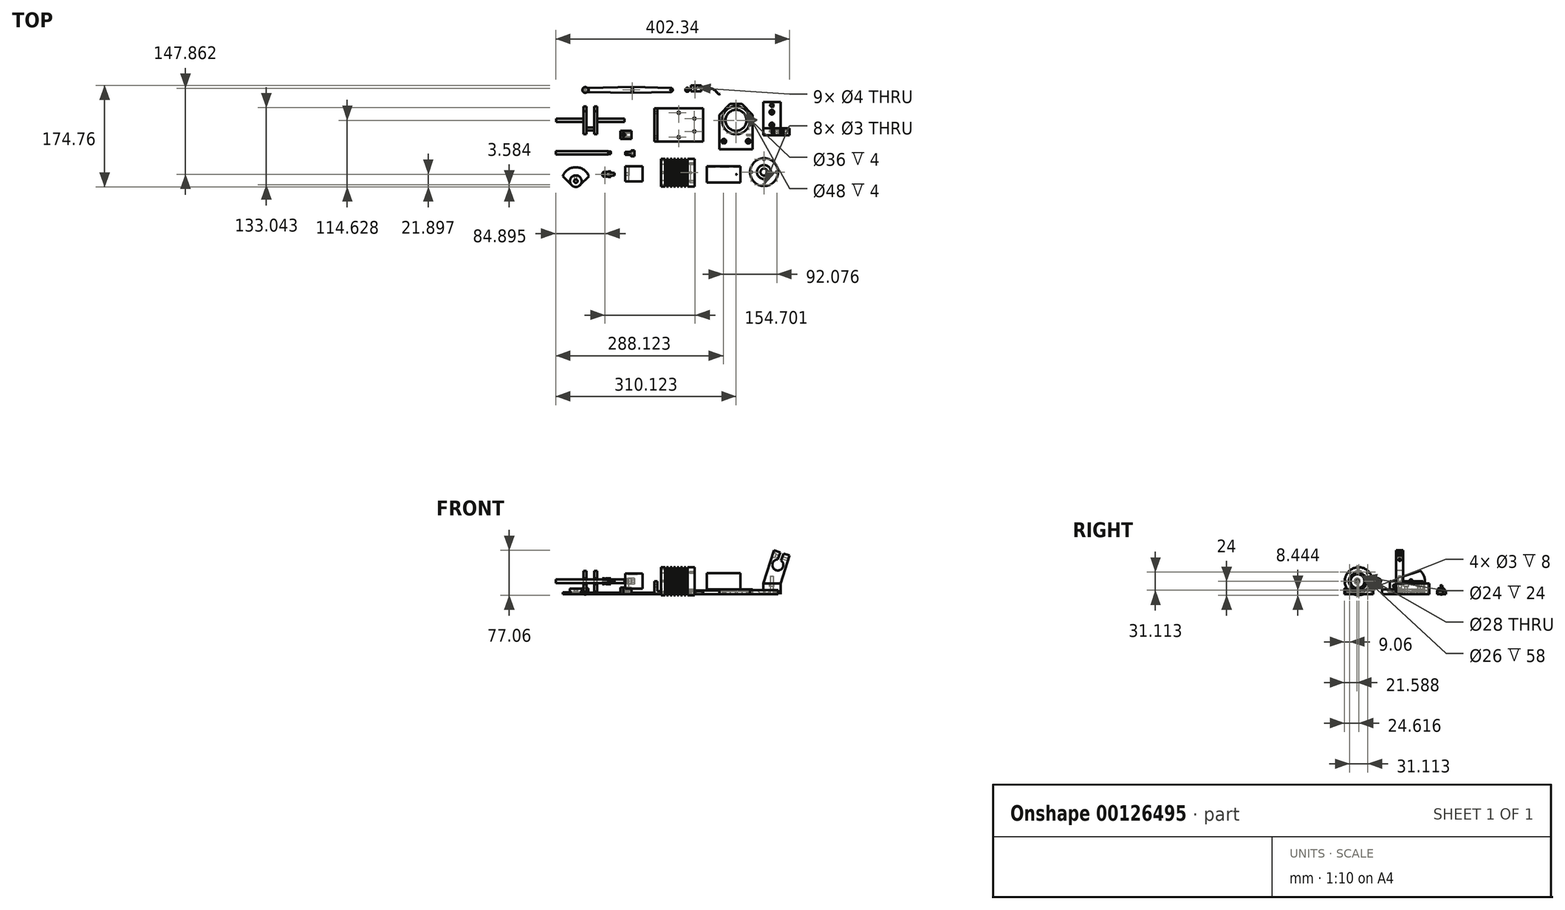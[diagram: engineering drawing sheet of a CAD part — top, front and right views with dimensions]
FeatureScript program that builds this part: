
annotation { "Feature Type Name" : "Feature", "Feature Type Description" : "" }
export const myFeature = defineFeature(function(context is Context, id is Id, definition is map)
    precondition{}
    {
        {
            var Q0;
            Q0=qCreatedBy(makeId("Top.planeOp"),FACE);
            var sketch = newSketch(context, id + "F0", { "sketchPlane" : qUnion([Q0])});
            skLineSegment(sketch, "E0.bottom", {"start": v(-42, 28.5) * mm, "end": v(42, 28.5) * mm});
            skLineSegment(sketch, "E0.top", {"start": v(-42, -28.5) * mm, "end": v(42, -28.5) * mm});
            skLineSegment(sketch, "E0.left", {"start": v(-42, 28.5) * mm, "end": v(-42, -28.5) * mm});
            skLineSegment(sketch, "E0.right", {"start": v(42, 28.5) * mm, "end": v(42, -28.5) * mm});
            skLineSegment(sketch, "E1", {"start": v(42, 0) * mm, "end": v(-42, 0) * mm, "construction": true});
            skLineSegment(sketch, "E2.0", {"start": v(27, 28.5) * mm, "end": v(27, -28.5) * mm, "construction": true});
            skLineSegment(sketch, "E3.0", {"start": v(0, 28.5) * mm, "end": v(0, -28.5) * mm, "construction": true});
            skCircle(sketch, "E4", {"center": v(27, 11) * mm, "radius": 2 * mm});
            skCircle(sketch, "E5", {"center": v(0, 21) * mm, "radius": 2 * mm});
            skCircle(sketch, "E6.MirrorC", {"center": v(27, -11) * mm, "radius": 2 * mm});
            skCircle(sketch, "E7.MirrorC", {"center": v(0, -21) * mm, "radius": 2 * mm});
            skSolve(sketch);
        }
        {
            var Q0;
            Q0=makeQuery(id+"F0.imprint","IMPRINT",FACE,{"disambiguationData":[TD([[makeQuery(id+"F0.imprint","IMPRINT",EDGE,{"derivedFrom":sQuery(id+"F0.wireOp",EDGE,"E0.bottom")}),-1.0]])]});
            var Q1;
            Q1 = qConstructionFilter(qBodyType(qCreatedBy(id + "F0" ,EDGE), BodyType.WIRE), ConstructionObject.NO);
            extrude(context, id + "F1", {"entities" : qUnion([Q0]), "surfaceEntities" : qUnion([Q1]), "depth" : 5 * mm});
        }
        {
            var Q0;
            Q0=makeQuery(id+"F1.opExtrude","CAP_FACE",FACE,{"disambiguationData":[OSD([sQuery(id+"F0.wireOp",EDGE,"E0.bottom"),sQuery(id+"F0.wireOp",EDGE,"E0.top"),sQuery(id+"F0.wireOp",EDGE,"E0.left"),sQuery(id+"F0.wireOp",EDGE,"E0.right"),sQuery(id+"F0.wireOp",EDGE,"E4"),sQuery(id+"F0.wireOp",EDGE,"E5"),sQuery(id+"F0.wireOp",EDGE,"E6.MirrorC"),sQuery(id+"F0.wireOp",EDGE,"E7.MirrorC")])],"isStart":true});
            var sketch = newSketch(context, id + "F2", { "sketchPlane" : qUnion([Q0])});
            skLineSegment(sketch, "E8.bottom", {"start": v(-42, 28.5) * mm, "end": v(-37, 28.5) * mm});
            skLineSegment(sketch, "E8.top", {"start": v(-42, -28.5) * mm, "end": v(-37, -28.5) * mm});
            skLineSegment(sketch, "E8.left", {"start": v(-42, 28.5) * mm, "end": v(-42, -28.5) * mm});
            skLineSegment(sketch, "E8.right", {"start": v(-37, 28.5) * mm, "end": v(-37, -28.5) * mm});
            skSolve(sketch);
        }
        {
            var Q0;
            Q0 = qSketchRegion(id + "F2", true);
            extrude(context, id + "F3", {"entities" : qUnion([Q0]), "operationType" : NewBodyOperationType.ADD, "oppositeDirection" : true, "depth" : 22 * mm});
        }
        {
            var Q0;
            Q0=makeQuery(id+"F3.boolean.opBoolean","MERGE",FACE,{"derivedFrom":[makeQuery(id+"F1.opExtrude","SWEPT_FACE",FACE,{"disambiguationData":[OSD([sQuery(id+"F0.wireOp",EDGE,"E0.left")])]}),makeQuery(id+"F3.opExtrude","SWEPT_FACE",FACE,{"disambiguationData":[OSD([sQuery(id+"F2.wireOp",EDGE,"E8.left")])]})]});
            var sketch = newSketch(context, id + "F4", { "sketchPlane" : qUnion([Q0])});
            skLineSegment(sketch, "E9.0", {"start": v(-28.5, 14) * mm, "end": v(28.5, 14) * mm, "construction": true});
            skLineSegment(sketch, "E10", {"start": v(0, 0) * mm, "end": v(0, 22) * mm, "construction": true});
            skCircle(sketch, "E11", {"center": v(-21, 14) * mm, "radius": 2 * mm});
            skCircle(sketch, "E12.MirrorC", {"center": v(21, 14) * mm, "radius": 2 * mm});
            skSolve(sketch);
        }
        {
            var Q0;
            Q0 = qSketchRegion(id + "F4", true);
            var Q1;
            Q1=makeQuery(id+"F3.opExtrude","SWEPT_FACE",FACE,{"disambiguationData":[OSD([sQuery(id+"F2.wireOp",EDGE,"E8.right")])]});
            extrude(context, id + "F5", {"entities" : qUnion([Q0]), "operationType" : NewBodyOperationType.REMOVE, "endBound" : BoundingType.UP_TO_SURFACE, "oppositeDirection" : true, "endBoundEntityFace" : qUnion([Q1]), "depth" : 25 * mm});
        }
        {
            var Q0;
            Q0=qCreatedBy(makeId("Top.planeOp"),FACE);
            var sketch = newSketch(context, id + "F6", { "sketchPlane" : qUnion([Q0])});
            skLineSegment(sketch, "E13", {"start": v(70.12, -41.96) * mm, "end": v(127.12, -41.96) * mm});
            skLineSegment(sketch, "E14", {"start": v(127.12, -41.96) * mm, "end": v(127.12, 17.54) * mm});
            skLineSegment(sketch, "E15", {"start": v(127.12, 17.54) * mm, "end": v(108.62, 36.04) * mm});
            skLineSegment(sketch, "E16", {"start": v(108.62, 36.04) * mm, "end": v(88.62, 36.04) * mm});
            skLineSegment(sketch, "E17", {"start": v(88.62, 36.04) * mm, "end": v(70.12, 17.54) * mm});
            skLineSegment(sketch, "E18", {"start": v(70.12, 17.54) * mm, "end": v(70.12, -41.96) * mm});
            skLineSegment(sketch, "E19", {"start": v(98.62, -41.96) * mm, "end": v(98.62, 36.04) * mm, "construction": true});
            skLineSegment(sketch, "E20.0", {"start": v(70.12, 8.04) * mm, "end": v(127.12, 8.04) * mm, "construction": true});
            skCircle(sketch, "E21", {"center": v(98.62, 8.04) * mm, "radius": 18 * mm});
            skLineSegment(sketch, "E22.0", {"start": v(70.12, -27.96) * mm, "end": v(127.12, -27.96) * mm, "construction": true});
            skCircle(sketch, "E23", {"center": v(119.62, -27.96) * mm, "radius": 2.1 * mm});
            skCircle(sketch, "E24.MirrorC", {"center": v(77.62, -27.96) * mm, "radius": 2.1 * mm});
            skCircle(sketch, "E25", {"center": v(98.62, 8.04) * mm, "radius": 22 * mm, "construction": true});
            skCircle(sketch, "E26", {"center": v(98.62, 30.04) * mm, "radius": 1.5 * mm});
            skCircle(sketch, "E27", {"center": v(120.62, 8.04) * mm, "radius": 1.5 * mm});
            skCircle(sketch, "E28", {"center": v(98.62, -13.96) * mm, "radius": 1.5 * mm});
            skCircle(sketch, "E29", {"center": v(76.62, 8.04) * mm, "radius": 1.5 * mm});
            skSolve(sketch);
        }
        {
            var Q0;
            Q0 = qSketchRegion(id + "F6", true);
            extrude(context, id + "F7", {"entities" : qUnion([Q0]), "depth" : 8 * mm});
        }
        {
            var Q0;
            Q0=makeQuery(id+"F7.opExtrude","CAP_FACE",FACE,{"disambiguationData":[OSD([sQuery(id+"F6.wireOp",EDGE,"E13"),sQuery(id+"F6.wireOp",EDGE,"E14"),sQuery(id+"F6.wireOp",EDGE,"E15"),sQuery(id+"F6.wireOp",EDGE,"E16"),sQuery(id+"F6.wireOp",EDGE,"E17"),sQuery(id+"F6.wireOp",EDGE,"E18"),sQuery(id+"F6.wireOp",EDGE,"E21"),sQuery(id+"F6.wireOp",EDGE,"E23"),sQuery(id+"F6.wireOp",EDGE,"E24.MirrorC"),sQuery(id+"F6.wireOp",EDGE,"E26"),sQuery(id+"F6.wireOp",EDGE,"E27"),sQuery(id+"F6.wireOp",EDGE,"E28"),sQuery(id+"F6.wireOp",EDGE,"E29")])],"isStart":false});
            var sketch = newSketch(context, id + "F8", { "sketchPlane" : qUnion([Q0])});
            skCircle(sketch, "E30", {"center": v(77.62, -27.96) * mm, "radius": 4 * mm});
            skCircle(sketch, "E31", {"center": v(119.62, -27.96) * mm, "radius": 4 * mm});
            skCircle(sketch, "E32", {"center": v(98.62, 8.04) * mm, "radius": 24 * mm});
            skSolve(sketch);
        }
        {
            var Q0;
            Q0 = qSketchRegion(id + "F8", true);
            extrude(context, id + "F9", {"entities" : qUnion([Q0]), "operationType" : NewBodyOperationType.REMOVE, "oppositeDirection" : true, "depth" : 4 * mm});
        }
        {
            var Q0;
            Q0=makeQuery(id+"F7.opExtrude","SWEPT_FACE",FACE,{"disambiguationData":[OSD([sQuery(id+"F6.wireOp",EDGE,"E14")])]});
            var sketch = newSketch(context, id + "F10", { "sketchPlane" : qUnion([Q0])});
            skLineSegment(sketch, "E33", {"start": v(-41.96, 4) * mm, "end": v(-16.96, 4) * mm, "construction": true});
            skCircle(sketch, "E34", {"center": v(-16.96, 4) * mm, "radius": 1.5 * mm});
            skSolve(sketch);
        }
        {
            var Q0;
            Q0 = qSketchRegion(id + "F10", true);
            extrude(context, id + "F11", {"entities" : qUnion([Q0]), "operationType" : NewBodyOperationType.REMOVE, "oppositeDirection" : true, "depth" : 10 * mm});
        }
        {
            var Q0;
            Q0=makeQuery(id+"F3.opExtrude","CAP_FACE",FACE,{"disambiguationData":[OSD([sQuery(id+"F2.wireOp",EDGE,"E8.bottom"),sQuery(id+"F2.wireOp",EDGE,"E8.top"),sQuery(id+"F2.wireOp",EDGE,"E8.left"),sQuery(id+"F2.wireOp",EDGE,"E8.right")])],"isStart":false});
            var sketch = newSketch(context, id + "F12", { "sketchPlane" : qUnion([Q0])});
            skLineSegment(sketch, "E35", {"start": v(-30.6, -81.97) * mm, "end": v(27.4, -81.97) * mm, "construction": true});
            skLineSegment(sketch, "E36.0", {"start": v(-30.6, -67.97) * mm, "end": v(27.4, -67.97) * mm});
            skLineSegment(sketch, "E37.0", {"start": v(-30.6, -57.97) * mm, "end": v(-23.6, -57.97) * mm});
            skLineSegment(sketch, "E38", {"start": v(-30.6, -57.97) * mm, "end": v(-30.6, -67.97) * mm});
            skLineSegment(sketch, "E39", {"start": v(27.4, -57.97) * mm, "end": v(27.4, -67.97) * mm});
            skLineSegment(sketch, "E40.0", {"start": v(-23.6, -63.97) * mm, "end": v(-20.6, -63.97) * mm});
            skLineSegment(sketch, "E41.0", {"start": v(-23.6, -57.97) * mm, "end": v(-23.6, -63.97) * mm});
            skLineSegment(sketch, "E42.0", {"start": v(-20.6, -57.97) * mm, "end": v(-20.6, -63.97) * mm});
            skLineSegment(sketch, "E43.0", {"start": v(-17.6, -57.97) * mm, "end": v(-17.6, -63.97) * mm});
            skLineSegment(sketch, "E44.0", {"start": v(-14.6, -57.97) * mm, "end": v(-14.6, -63.97) * mm});
            skLineSegment(sketch, "E45.0", {"start": v(-11.6, -57.97) * mm, "end": v(-11.6, -63.97) * mm});
            skLineSegment(sketch, "E46.0", {"start": v(-8.6, -57.97) * mm, "end": v(-8.6, -63.97) * mm});
            skLineSegment(sketch, "E47.0", {"start": v(-5.6, -57.97) * mm, "end": v(-5.6, -63.97) * mm});
            skLineSegment(sketch, "E48.0", {"start": v(-2.6, -57.97) * mm, "end": v(-2.6, -63.97) * mm});
            skLineSegment(sketch, "E49.0", {"start": v(0.4, -57.97) * mm, "end": v(0.4, -63.97) * mm});
            skLineSegment(sketch, "E50.0", {"start": v(3.4, -57.97) * mm, "end": v(3.4, -63.97) * mm});
            skLineSegment(sketch, "E51.0", {"start": v(6.4, -57.97) * mm, "end": v(6.4, -63.97) * mm});
            skLineSegment(sketch, "E52.0", {"start": v(9.4, -57.97) * mm, "end": v(9.4, -63.97) * mm});
            skLineSegment(sketch, "E53.trimOffspring", {"start": v(-20.6, -57.97) * mm, "end": v(-17.6, -57.97) * mm});
            skLineSegment(sketch, "E54.trimOffspring", {"start": v(-17.6, -63.97) * mm, "end": v(-14.6, -63.97) * mm});
            skLineSegment(sketch, "E55.trimOffspring", {"start": v(-14.6, -57.97) * mm, "end": v(-11.6, -57.97) * mm});
            skLineSegment(sketch, "E56.trimOffspring", {"start": v(-8.6, -57.97) * mm, "end": v(-5.6, -57.97) * mm});
            skLineSegment(sketch, "E57.trimOffspring", {"start": v(-2.6, -57.97) * mm, "end": v(0.4, -57.97) * mm});
            skLineSegment(sketch, "E58.trimOffspring", {"start": v(3.4, -57.97) * mm, "end": v(6.4, -57.97) * mm});
            skLineSegment(sketch, "E59.trimOffspring", {"start": v(9.4, -57.97) * mm, "end": v(12.4, -57.97) * mm});
            skLineSegment(sketch, "E60.0", {"start": v(12.4, -57.97) * mm, "end": v(12.4, -63.97) * mm});
            skLineSegment(sketch, "E61.0", {"start": v(15.4, -57.97) * mm, "end": v(15.4, -63.97) * mm});
            skLineSegment(sketch, "E62.trimOffspring", {"start": v(15.4, -57.97) * mm, "end": v(27.4, -57.97) * mm});
            skLineSegment(sketch, "E63.trimOffspring", {"start": v(-11.6, -63.97) * mm, "end": v(-8.6, -63.97) * mm});
            skLineSegment(sketch, "E64.trimOffspring", {"start": v(-5.6, -63.97) * mm, "end": v(-2.6, -63.97) * mm});
            skLineSegment(sketch, "E65.trimOffspring", {"start": v(0.4, -63.97) * mm, "end": v(3.4, -63.97) * mm});
            skLineSegment(sketch, "E66.trimOffspring", {"start": v(6.4, -63.97) * mm, "end": v(9.4, -63.97) * mm});
            skLineSegment(sketch, "E67.trimOffspring", {"start": v(12.4, -63.97) * mm, "end": v(15.4, -63.97) * mm});
            skSolve(sketch);
        }
        {
            var Q0;
            Q0 = qSketchRegion(id + "F12", true);
            var Q1;
            Q1=sQuery(id+"F12.wireOp",EDGE,"E35");
            revolve(context, id + "F13", {"entities" : qUnion([Q0]), "axis" : qUnion([Q1]), "revolveType" : RevolveType.FULL});
        }
        {
            var Q0;
            Q0=qCreatedBy(makeId("Top.planeOp"),FACE);
            var sketch = newSketch(context, id + "F14", { "sketchPlane" : qUnion([Q0])});
            skLineSegment(sketch, "E68", {"start": v(15.4, -91.57) * mm, "end": v(27.4, -91.57) * mm, "construction": true});
            skLineSegment(sketch, "E69", {"start": v(27.4, -72.38) * mm, "end": v(15.4, -72.38) * mm, "construction": true});
            skLineSegment(sketch, "E70", {"start": v(27.4, -72.38) * mm, "end": v(27.4, -91.57) * mm, "construction": true});
            skLineSegment(sketch, "E71", {"start": v(27.4, -81.97) * mm, "end": v(20.4, -81.97) * mm, "construction": true});
            skCircle(sketch, "E72", {"center": v(20.4, -81.97) * mm, "radius": 2 * mm});
            skSolve(sketch);
        }
        {
            var Q0;
            Q0 = qSketchRegion(id + "F14", true);
            extrude(context, id + "F15", {"entities" : qUnion([Q0]), "operationType" : NewBodyOperationType.REMOVE, "endBound" : BoundingType.SYMMETRIC, "oppositeDirection" : true, "depth" : 29.23 * mm});
        }
        {
            var Q0;
            Q0=makeQuery(id+"F13.opRevolve","SWEPT_FACE",FACE,{"disambiguationData":[OSD([sQuery(id+"F12.wireOp",EDGE,"E38")])]});
            var sketch = newSketch(context, id + "F16", { "sketchPlane" : qUnion([Q0])});
            skCircle(sketch, "E73", {"center": v(81.97, 22) * mm, "radius": 22 * mm, "construction": true});
            skCircle(sketch, "E74", {"center": v(59.97, 22) * mm, "radius": 1.5 * mm});
            skCircle(sketch, "E75", {"center": v(103.97, 22) * mm, "radius": 1.5 * mm});
            skCircle(sketch, "E76", {"center": v(81.97, 44) * mm, "radius": 1.5 * mm});
            skCircle(sketch, "E77", {"center": v(81.97, 0) * mm, "radius": 1.5 * mm});
            skSolve(sketch);
        }
        {
            var Q0;
            Q0 = qSketchRegion(id + "F16", true);
            extrude(context, id + "F17", {"entities" : qUnion([Q0]), "operationType" : NewBodyOperationType.REMOVE, "oppositeDirection" : true, "depth" : 5 * mm});
        }
        {
            var Q0;
            Q0=makeQuery(id+"F13.opRevolve","SWEPT_FACE",FACE,{"disambiguationData":[OSD([sQuery(id+"F12.wireOp",EDGE,"E39")])]});
            var sketch = newSketch(context, id + "F18", { "sketchPlane" : qUnion([Q0])});
            skCircle(sketch, "E78", {"center": v(-81.97, 22) * mm, "radius": 22 * mm, "construction": true});
            skLineSegment(sketch, "E79", {"start": v(-81.97, 22) * mm, "end": v(-66.42, 37.56) * mm, "construction": true});
            skLineSegment(sketch, "E80", {"start": v(-81.97, 22) * mm, "end": v(-81.97, 44) * mm, "construction": true});
            skLineSegment(sketch, "E81", {"start": v(-81.97, 22) * mm, "end": v(-66.42, 6.44) * mm, "construction": true});
            skCircle(sketch, "E82", {"center": v(-66.42, 37.56) * mm, "radius": 1.5 * mm});
            skCircle(sketch, "E83", {"center": v(-66.42, 6.44) * mm, "radius": 1.5 * mm});
            skCircle(sketch, "E84.MirrorC", {"center": v(-97.53, 37.56) * mm, "radius": 1.5 * mm});
            skCircle(sketch, "E85.MirrorC", {"center": v(-97.53, 6.44) * mm, "radius": 1.5 * mm});
            skSolve(sketch);
        }
        {
            var Q0;
            Q0 = qSketchRegion(id + "F18", true);
            extrude(context, id + "F19", {"entities" : qUnion([Q0]), "operationType" : NewBodyOperationType.REMOVE, "oppositeDirection" : true, "depth" : 8 * mm});
        }
        {
            var Q0;
            Q0=makeQuery(id+"F3.opExtrude","CAP_FACE",FACE,{"disambiguationData":[OSD([sQuery(id+"F2.wireOp",EDGE,"E8.bottom"),sQuery(id+"F2.wireOp",EDGE,"E8.top"),sQuery(id+"F2.wireOp",EDGE,"E8.left"),sQuery(id+"F2.wireOp",EDGE,"E8.right")])],"isStart":false});
            var sketch = newSketch(context, id + "F20", { "sketchPlane" : qUnion([Q0])});
            skLineSegment(sketch, "E86", {"start": v(106.23, -85) * mm, "end": v(48.23, -85) * mm, "construction": true});
            skLineSegment(sketch, "E87.0", {"start": v(106.23, -71) * mm, "end": v(48.23, -71) * mm});
            skLineSegment(sketch, "E88.0", {"start": v(106.23, -72) * mm, "end": v(48.23, -72) * mm});
            skLineSegment(sketch, "E89", {"start": v(106.23, -71) * mm, "end": v(106.23, -72) * mm});
            skLineSegment(sketch, "E90", {"start": v(48.23, -71) * mm, "end": v(48.23, -72) * mm});
            skSolve(sketch);
        }
        {
            var Q0;
            Q0 = qSketchRegion(id + "F20", true);
            var Q1;
            Q1=sQuery(id+"F20.wireOp",EDGE,"E86");
            revolve(context, id + "F21", {"entities" : qUnion([Q0]), "axis" : qUnion([Q1]), "revolveType" : RevolveType.FULL});
        }
        {
            var Q0;
            Q0=makeQuery(id+"F3.opExtrude","CAP_FACE",FACE,{"disambiguationData":[OSD([sQuery(id+"F2.wireOp",EDGE,"E8.bottom"),sQuery(id+"F2.wireOp",EDGE,"E8.top"),sQuery(id+"F2.wireOp",EDGE,"E8.left"),sQuery(id+"F2.wireOp",EDGE,"E8.right")])],"isStart":false});
            var sketch = newSketch(context, id + "F22", { "sketchPlane" : qUnion([Q0])});
            skLineSegment(sketch, "E91", {"start": v(99.23, -85) * mm, "end": v(106.23, -85) * mm, "construction": true});
            skCircle(sketch, "E92", {"center": v(99.23, -85) * mm, "radius": 0.5 * mm});
            skSolve(sketch);
        }
        {
            var Q0;
            Q0 = qSketchRegion(id + "F22", true);
            extrude(context, id + "F23", {"entities" : qUnion([Q0]), "operationType" : NewBodyOperationType.REMOVE, "depth" : 25 * mm});
        }
        {
            var Q0;
            Q0=qCreatedBy(makeId("Top.planeOp"),FACE);
            var sketch = newSketch(context, id + "F24", { "sketchPlane" : qUnion([Q0])});
            skCircle(sketch, "E93", {"center": v(146.7, -81) * mm, "radius": 24 * mm});
            skCircle(sketch, "E94", {"center": v(146.7, -81) * mm, "radius": 22 * mm, "construction": true});
            skCircle(sketch, "E95", {"center": v(146.7, -59) * mm, "radius": 1.5 * mm});
            skCircle(sketch, "E96.1.0", {"center": v(124.7, -81) * mm, "radius": 1.5 * mm});
            skCircle(sketch, "E96.2.0", {"center": v(146.7, -103) * mm, "radius": 1.5 * mm});
            skCircle(sketch, "E96.3.0", {"center": v(168.7, -81) * mm, "radius": 1.5 * mm});
            skCircle(sketch, "E97", {"center": v(146.7, -81) * mm, "radius": 6 * mm});
            skSolve(sketch);
        }
        {
            var Q0;
            Q0 = qSketchRegion(id + "F24", true);
            extrude(context, id + "F25", {"entities" : qUnion([Q0]), "depth" : 7 * mm});
        }
        {
            var Q0;
            Q0=makeQuery(id+"F25.opExtrude","CAP_EDGE",EDGE,{"disambiguationData":[OSD([sQuery(id+"F24.wireOp",EDGE,"E97")])],"isStart":false});
            chamfer(context, id + "F26", {"entities" : qUnion([Q0]), "width" : 6 * mm, "tangentPropagation" : true});
        }
        {
            var Q0;
            Q0=qCreatedBy(makeId("Top.planeOp"),FACE);
            var sketch = newSketch(context, id + "F27", { "sketchPlane" : qUnion([Q0])});
            skLineSegment(sketch, "E98.bottom", {"start": v(145.16, 39.54) * mm, "end": v(175.16, 39.54) * mm});
            skLineSegment(sketch, "E98.top", {"start": v(145.16, -17.46) * mm, "end": v(175.16, -17.46) * mm});
            skLineSegment(sketch, "E98.left", {"start": v(145.16, 39.54) * mm, "end": v(145.16, -17.46) * mm});
            skLineSegment(sketch, "E98.right", {"start": v(175.16, 39.54) * mm, "end": v(175.16, -17.46) * mm});
            skSolve(sketch);
        }
        {
            var Q0;
            Q0 = qSketchRegion(id + "F27", true);
            extrude(context, id + "F28", {"entities" : qUnion([Q0]), "depth" : 18 * mm});
        }
        {
            var Q0;
            Q0=makeQuery(id+"F28.opExtrude","SWEPT_FACE",FACE,{"disambiguationData":[OSD([sQuery(id+"F27.wireOp",EDGE,"E98.top")])]});
            var sketch = newSketch(context, id + "F29", { "sketchPlane" : qUnion([Q0])});
            skLineSegment(sketch, "E99", {"start": v(145.16, 18) * mm, "end": v(163.7, 75.06) * mm});
            skLineSegment(sketch, "E100", {"start": v(163.7, 75.06) * mm, "end": v(174.42, 71.58) * mm});
            skLineSegment(sketch, "E101", {"start": v(190.84, 66.25) * mm, "end": v(175.16, 18) * mm});
            skLineSegment(sketch, "E102", {"start": v(175.16, 18) * mm, "end": v(145.16, 18) * mm});
            skLineSegment(sketch, "E103.0", {"start": v(145.16, 50) * mm, "end": v(175.16, 50) * mm, "construction": true});
            skLineSegment(sketch, "E104", {"start": v(177.27, 70.66) * mm, "end": v(160.16, 18) * mm, "construction": true});
            skArc(sketch, "E105", {"start": v(170.5, 59.5) * mm, "mid": v(167.62, 40.96) * mm, "end": v(176.2, 57.65) * mm});
            skLineSegment(sketch, "E106.0", {"start": v(174.42, 71.58) * mm, "end": v(170.5, 59.5) * mm});
            skLineSegment(sketch, "E107.0", {"start": v(180.12, 69.73) * mm, "end": v(176.2, 57.65) * mm});
            skLineSegment(sketch, "E108.trimOffspring", {"start": v(180.12, 69.73) * mm, "end": v(190.84, 66.25) * mm});
            skSolve(sketch);
        }
        {
            var Q0;
            Q0 = qSketchRegion(id + "F29", true);
            extrude(context, id + "F30", {"entities" : qUnion([Q0]), "oppositeDirection" : true, "depth" : 12 * mm});
        }
        {
            var Q0;
            Q0=makeQuery(id+"F28.opExtrude","CAP_FACE",FACE,{"disambiguationData":[OSD([sQuery(id+"F27.wireOp",EDGE,"E98.bottom"),sQuery(id+"F27.wireOp",EDGE,"E98.top"),sQuery(id+"F27.wireOp",EDGE,"E98.left"),sQuery(id+"F27.wireOp",EDGE,"E98.right")])],"isStart":true});
            var sketch = newSketch(context, id + "F31", { "sketchPlane" : qUnion([Q0])});
            skLineSegment(sketch, "E109", {"start": v(160.16, -39.54) * mm, "end": v(160.16, 17.46) * mm, "construction": true});
            skLineSegment(sketch, "E110.0", {"start": v(145.16, -33.54) * mm, "end": v(175.16, -33.54) * mm, "construction": true});
            skLineSegment(sketch, "E111.0", {"start": v(145.16, 11.46) * mm, "end": v(175.16, 11.46) * mm, "construction": true});
            skCircle(sketch, "E112", {"center": v(160.16, -33.54) * mm, "radius": 4.5 * mm});
            skCircle(sketch, "E113", {"center": v(160.16, 11.46) * mm, "radius": 4.5 * mm});
            skSolve(sketch);
        }
        {
            var Q0;
            Q0 = qSketchRegion(id + "F31", true);
            extrude(context, id + "F32", {"entities" : qUnion([Q0]), "operationType" : NewBodyOperationType.REMOVE, "oppositeDirection" : true, "depth" : 6 * mm});
        }
        {
            var Q0;
            Q0=makeQuery(id+"F32.boolean.opBoolean","COPY",FACE,{"derivedFrom":makeQuery(id+"F32.opExtrude","CAP_FACE",FACE,{"disambiguationData":[OSD([sQuery(id+"F31.wireOp",EDGE,"E112")])],"isStart":false})});
            var sketch = newSketch(context, id + "F33", { "sketchPlane" : qUnion([Q0])});
            skCircle(sketch, "E114", {"center": v(160.16, -33.54) * mm, "radius": 2.5 * mm});
            skLineSegment(sketch, "E115.0.0", {"start": v(145.16, -39.54) * mm, "end": v(175.16, -39.54) * mm, "construction": true});
            skLineSegment(sketch, "E115.0.1", {"start": v(175.16, -39.54) * mm, "end": v(175.16, 17.46) * mm, "construction": true});
            skLineSegment(sketch, "E115.0.2", {"start": v(175.16, 17.46) * mm, "end": v(145.16, 17.46) * mm, "construction": true});
            skLineSegment(sketch, "E115.0.3", {"start": v(145.16, 17.46) * mm, "end": v(145.16, -39.54) * mm, "construction": true});
            skLineSegment(sketch, "E116", {"start": v(145.16, -11.04) * mm, "end": v(175.16, -11.04) * mm, "construction": true});
            skCircle(sketch, "E117.MirrorC", {"center": v(160.16, 11.46) * mm, "radius": 2.5 * mm});
            skSolve(sketch);
        }
        {
            var Q0;
            Q0 = qSketchRegion(id + "F33", true);
            extrude(context, id + "F34", {"entities" : qUnion([Q0]), "operationType" : NewBodyOperationType.REMOVE, "oppositeDirection" : true, "depth" : 25 * mm});
        }
        {
            var Q0;
            Q0=makeQuery(id+"F30.opExtrude","SWEPT_FACE",FACE,{"disambiguationData":[OSD([sQuery(id+"F29.wireOp",EDGE,"E99")])]});
            var sketch = newSketch(context, id + "F35", { "sketchPlane" : qUnion([Q0])});
            skLineSegment(sketch, "E118.0.0", {"start": v(17.46, 61.98) * mm, "end": v(17.46, 121.98) * mm, "construction": true});
            skLineSegment(sketch, "E118.0.1", {"start": v(17.46, 121.98) * mm, "end": v(5.46, 121.98) * mm, "construction": true});
            skLineSegment(sketch, "E118.0.2", {"start": v(5.46, 121.98) * mm, "end": v(5.46, 61.98) * mm, "construction": true});
            skLineSegment(sketch, "E118.0.3", {"start": v(5.46, 61.98) * mm, "end": v(17.46, 61.98) * mm, "construction": true});
            skLineSegment(sketch, "E119", {"start": v(11.46, 121.98) * mm, "end": v(11.46, 113.98) * mm, "construction": true});
            skCircle(sketch, "E120", {"center": v(11.46, 113.98) * mm, "radius": 4 * mm});
            skSolve(sketch);
        }
        {
            var Q0;
            Q0 = qSketchRegion(id + "F35", true);
            extrude(context, id + "F36", {"entities" : qUnion([Q0]), "operationType" : NewBodyOperationType.REMOVE, "oppositeDirection" : true, "depth" : 5 * mm});
        }
        {
            var Q0;
            Q0=makeQuery(id+"F36.boolean.opBoolean","COPY",FACE,{"derivedFrom":makeQuery(id+"F36.opExtrude","CAP_FACE",FACE,{"disambiguationData":[OSD([sQuery(id+"F35.wireOp",EDGE,"E120")])],"isStart":false})});
            var sketch = newSketch(context, id + "F37", { "sketchPlane" : qUnion([Q0])});
            skCircle(sketch, "E121", {"center": v(11.46, 113.98) * mm, "radius": 2 * mm});
            skSolve(sketch);
        }
        {
            var Q0;
            Q0 = qSketchRegion(id + "F37", true);
            var Q1;
            Q1=makeQuery(id+"F30.opExtrude","SWEPT_FACE",FACE,{"disambiguationData":[OSD([sQuery(id+"F29.wireOp",EDGE,"E101")])]});
            extrude(context, id + "F38", {"entities" : qUnion([Q0]), "operationType" : NewBodyOperationType.REMOVE, "endBound" : BoundingType.UP_TO_SURFACE, "oppositeDirection" : true, "endBoundEntityFace" : qUnion([Q1]), "depth" : 25 * mm});
        }
        {
            var Q0;
            Q0=makeQuery(id+"F28.opExtrude","CAP_FACE",FACE,{"disambiguationData":[OSD([sQuery(id+"F27.wireOp",EDGE,"E98.bottom"),sQuery(id+"F27.wireOp",EDGE,"E98.top"),sQuery(id+"F27.wireOp",EDGE,"E98.left"),sQuery(id+"F27.wireOp",EDGE,"E98.right")])],"isStart":false});
            var sketch = newSketch(context, id + "F39", { "sketchPlane" : qUnion([Q0])});
            skLineSegment(sketch, "E122.0.0", {"start": v(175.16, 39.54) * mm, "end": v(145.16, 39.54) * mm, "construction": true});
            skLineSegment(sketch, "E122.0.1", {"start": v(145.16, 39.54) * mm, "end": v(145.16, -17.46) * mm, "construction": true});
            skLineSegment(sketch, "E122.0.2", {"start": v(145.16, -17.46) * mm, "end": v(175.16, -17.46) * mm, "construction": true});
            skLineSegment(sketch, "E122.0.3", {"start": v(175.16, -17.46) * mm, "end": v(175.16, 39.54) * mm, "construction": true});
            skLineSegment(sketch, "E123", {"start": v(175.16, 11.04) * mm, "end": v(145.16, 11.04) * mm, "construction": true});
            skLineSegment(sketch, "E124.0", {"start": v(175.16, 0.04) * mm, "end": v(145.16, 0.04) * mm, "construction": true});
            skCircle(sketch, "E125", {"center": v(160.16, 0.04) * mm, "radius": 4 * mm});
            skCircle(sketch, "E126.MirrorC", {"center": v(160.16, 22.04) * mm, "radius": 4 * mm});
            skSolve(sketch);
        }
        {
            var Q0;
            Q0 = qSketchRegion(id + "F39", true);
            extrude(context, id + "F40", {"entities" : qUnion([Q0]), "operationType" : NewBodyOperationType.REMOVE, "oppositeDirection" : true, "depth" : 5 * mm});
        }
        {
            var Q0;
            Q0=makeQuery(id+"F40.boolean.opBoolean","COPY",FACE,{"derivedFrom":makeQuery(id+"F40.opExtrude","CAP_FACE",FACE,{"disambiguationData":[OSD([sQuery(id+"F39.wireOp",EDGE,"E125")])],"isStart":false})});
            var sketch = newSketch(context, id + "F41", { "sketchPlane" : qUnion([Q0])});
            skCircle(sketch, "E127", {"center": v(160.16, 0.04) * mm, "radius": 2.25 * mm});
            skLineSegment(sketch, "E128.0.0", {"start": v(175.16, 39.54) * mm, "end": v(145.16, 39.54) * mm, "construction": true});
            skLineSegment(sketch, "E128.0.1", {"start": v(145.16, 39.54) * mm, "end": v(145.16, -17.46) * mm, "construction": true});
            skLineSegment(sketch, "E128.0.2", {"start": v(145.16, -17.46) * mm, "end": v(175.16, -17.46) * mm, "construction": true});
            skLineSegment(sketch, "E128.0.3", {"start": v(175.16, -17.46) * mm, "end": v(175.16, 39.54) * mm, "construction": true});
            skLineSegment(sketch, "E129", {"start": v(145.16, 11.04) * mm, "end": v(175.16, 11.04) * mm, "construction": true});
            skCircle(sketch, "E130.MirrorC", {"center": v(160.16, 22.04) * mm, "radius": 2.25 * mm});
            skSolve(sketch);
        }
        {
            var Q0;
            Q0 = qSketchRegion(id + "F41", true);
            extrude(context, id + "F42", {"entities" : qUnion([Q0]), "operationType" : NewBodyOperationType.REMOVE, "oppositeDirection" : true, "depth" : 25 * mm});
        }
        {
            var Q0;
            Q0=makeQuery(id+"F3.opExtrude","CAP_FACE",FACE,{"disambiguationData":[OSD([sQuery(id+"F2.wireOp",EDGE,"E8.bottom"),sQuery(id+"F2.wireOp",EDGE,"E8.top"),sQuery(id+"F2.wireOp",EDGE,"E8.left"),sQuery(id+"F2.wireOp",EDGE,"E8.right")])],"isStart":false});
            var sketch = newSketch(context, id + "F43", { "sketchPlane" : qUnion([Q0])});
            skLineSegment(sketch, "E131", {"start": v(-61.96, -83.9) * mm, "end": v(-91.96, -83.9) * mm, "construction": true});
            skLineSegment(sketch, "E132.0", {"start": v(-61.96, -70.9) * mm, "end": v(-91.96, -70.9) * mm});
            skLineSegment(sketch, "E133.0", {"start": v(-61.96, -71.9) * mm, "end": v(-85.96, -71.9) * mm});
            skLineSegment(sketch, "E134.0", {"start": v(-85.96, -81.9) * mm, "end": v(-91.96, -81.9) * mm});
            skLineSegment(sketch, "E135", {"start": v(-91.96, -81.9) * mm, "end": v(-91.96, -70.9) * mm});
            skLineSegment(sketch, "E136.0", {"start": v(-85.96, -81.9) * mm, "end": v(-85.96, -71.9) * mm});
            skLineSegment(sketch, "E137", {"start": v(-61.96, -70.9) * mm, "end": v(-61.96, -71.9) * mm});
            skSolve(sketch);
        }
        {
            var Q0;
            Q0 = qSketchRegion(id + "F43", true);
            var Q1;
            Q1=sQuery(id+"F43.wireOp",EDGE,"E131");
            revolve(context, id + "F44", {"entities" : qUnion([Q0]), "axis" : qUnion([Q1]), "revolveType" : RevolveType.FULL});
        }
        {
            var Q0;
            Q0=makeQuery(id+"F3.opExtrude","CAP_FACE",FACE,{"disambiguationData":[OSD([sQuery(id+"F2.wireOp",EDGE,"E8.bottom"),sQuery(id+"F2.wireOp",EDGE,"E8.top"),sQuery(id+"F2.wireOp",EDGE,"E8.left"),sQuery(id+"F2.wireOp",EDGE,"E8.right")])],"isStart":false});
            var sketch = newSketch(context, id + "F45", { "sketchPlane" : qUnion([Q0])});
            skLineSegment(sketch, "E138", {"start": v(-131.6, -84.7) * mm, "end": v(-110.6, -84.7) * mm});
            skLineSegment(sketch, "E139.0", {"start": v(-116.6, -86.7) * mm, "end": v(-110.6, -86.7) * mm});
            skLineSegment(sketch, "E140.0", {"start": v(-131.6, -89.7) * mm, "end": v(-116.6, -89.7) * mm});
            skLineSegment(sketch, "E141", {"start": v(-110.6, -84.7) * mm, "end": v(-110.6, -86.7) * mm});
            skLineSegment(sketch, "E142.0", {"start": v(-116.6, -86.7) * mm, "end": v(-116.6, -89.7) * mm});
            skLineSegment(sketch, "E143", {"start": v(-131.6, -84.7) * mm, "end": v(-131.6, -89.7) * mm});
            skSolve(sketch);
        }
        {
            var Q0;
            Q0 = qSketchRegion(id + "F45", true);
            var Q1;
            Q1=sQuery(id+"F45.wireOp",EDGE,"E138");
            revolve(context, id + "F46", {"entities" : qUnion([Q0]), "axis" : qUnion([Q1]), "revolveType" : RevolveType.FULL});
        }
        {
            var Q0;
            Q0=makeQuery(id+"F3.opExtrude","CAP_FACE",FACE,{"disambiguationData":[OSD([sQuery(id+"F2.wireOp",EDGE,"E8.bottom"),sQuery(id+"F2.wireOp",EDGE,"E8.top"),sQuery(id+"F2.wireOp",EDGE,"E8.left"),sQuery(id+"F2.wireOp",EDGE,"E8.right")])],"isStart":false});
            var sketch = newSketch(context, id + "F47", { "sketchPlane" : qUnion([Q0])});
            skLineSegment(sketch, "E144", {"start": v(-131.6, -79.7) * mm, "end": v(-131.6, -89.7) * mm, "construction": true});
            skArc(sketch, "E145", {"start": v(-126.6, -79.7) * mm, "mid": v(-131.6, -84.7) * mm, "end": v(-126.6, -89.7) * mm});
            skPoint(sketch, "E145.centerSnap0", {"position": v(-131.6, -84.7) * mm});
            skLineSegment(sketch, "E146.bottom", {"start": v(-126.6, -89.7) * mm, "end": v(-135, -89.7) * mm});
            skLineSegment(sketch, "E146.top", {"start": v(-126.6, -79.7) * mm, "end": v(-135, -79.7) * mm});
            skLineSegment(sketch, "E146.right", {"start": v(-135, -89.7) * mm, "end": v(-135, -79.7) * mm});
            skSolve(sketch);
        }
        {
            var Q0;
            Q0 = qSketchRegion(id + "F47", true);
            extrude(context, id + "F48", {"entities" : qUnion([Q0]), "operationType" : NewBodyOperationType.REMOVE, "endBound" : BoundingType.THROUGH_ALL, "oppositeDirection" : true, "depth" : 25 * mm, "hasSecondDirection" : true, "secondDirectionOppositeDirection" : false, "secondDirectionDepth" : 25 * mm});
        }
        {
            var Q0;
            Q0=makeQuery(id+"F3.opExtrude","CAP_FACE",FACE,{"disambiguationData":[OSD([sQuery(id+"F2.wireOp",EDGE,"E8.bottom"),sQuery(id+"F2.wireOp",EDGE,"E8.top"),sQuery(id+"F2.wireOp",EDGE,"E8.left"),sQuery(id+"F2.wireOp",EDGE,"E8.right")])],"isStart":false});
            var sketch = newSketch(context, id + "F49", { "sketchPlane" : qUnion([Q0])});
            skArc(sketch, "E147", {"start": v(-126.6, -79.7) * mm, "mid": v(-131.6, -84.7) * mm, "end": v(-126.6, -89.7) * mm, "construction": true});
            skLineSegment(sketch, "E148", {"start": v(-126.6, -79.7) * mm, "end": v(-126.6, -89.7) * mm, "construction": true});
            skLineSegment(sketch, "E149.0", {"start": v(-120.6, -79.7) * mm, "end": v(-120.6, -89.7) * mm, "construction": true});
            skLineSegment(sketch, "E150.bottom", {"start": v(-136.69, -75.23) * mm, "end": v(-120.6, -75.23) * mm});
            skLineSegment(sketch, "E150.top", {"start": v(-136.69, -94.72) * mm, "end": v(-120.6, -94.72) * mm});
            skLineSegment(sketch, "E150.left", {"start": v(-136.69, -75.23) * mm, "end": v(-136.69, -94.72) * mm});
            skLineSegment(sketch, "E150.right", {"start": v(-120.6, -75.23) * mm, "end": v(-120.6, -94.72) * mm});
            skSolve(sketch);
        }
        {
            var Q0;
            Q0 = qSketchRegion(id + "F49", true);
            extrude(context, id + "F50", {"entities" : qUnion([Q0]), "operationType" : NewBodyOperationType.REMOVE, "depth" : 2.5 * mm, "hasSecondDirection" : true, "secondDirectionOppositeDirection" : true, "secondDirectionDepth" : 2.5 * mm});
        }
        {
            var Q0;
            Q0=makeQuery(id+"F3.opExtrude","CAP_FACE",FACE,{"disambiguationData":[OSD([sQuery(id+"F2.wireOp",EDGE,"E8.bottom"),sQuery(id+"F2.wireOp",EDGE,"E8.top"),sQuery(id+"F2.wireOp",EDGE,"E8.left"),sQuery(id+"F2.wireOp",EDGE,"E8.right")])],"isStart":false});
            var sketch = newSketch(context, id + "F51", { "sketchPlane" : qUnion([Q0])});
            skCircle(sketch, "E151", {"center": v(-126.6, -84.7) * mm, "radius": 2 * mm});
            skSolve(sketch);
        }
        {
            var Q0;
            Q0 = qSketchRegion(id + "F51", true);
            extrude(context, id + "F52", {"entities" : qUnion([Q0]), "operationType" : NewBodyOperationType.REMOVE, "endBound" : BoundingType.THROUGH_ALL, "depth" : 25 * mm, "hasSecondDirection" : true, "secondDirectionBound" : SecondDirectionBoundingType.THROUGH_ALL, "secondDirectionOppositeDirection" : true, "secondDirectionDepth" : 25 * mm});
        }
        {
            var Q0;
            Q0=makeQuery(id+"F3.opExtrude","CAP_FACE",FACE,{"disambiguationData":[OSD([sQuery(id+"F2.wireOp",EDGE,"E8.bottom"),sQuery(id+"F2.wireOp",EDGE,"E8.top"),sQuery(id+"F2.wireOp",EDGE,"E8.left"),sQuery(id+"F2.wireOp",EDGE,"E8.right")])],"isStart":false});
            var sketch = newSketch(context, id + "F53", { "sketchPlane" : qUnion([Q0])});
            skLineSegment(sketch, "E152.bottom", {"start": v(-91.92, -43.77) * mm, "end": v(-75.92, -43.77) * mm});
            skLineSegment(sketch, "E152.top", {"start": v(-91.92, -48.77) * mm, "end": v(-80.92, -48.77) * mm});
            skLineSegment(sketch, "E152.left", {"start": v(-91.92, -43.77) * mm, "end": v(-91.92, -48.77) * mm});
            skLineSegment(sketch, "E153.top", {"start": v(-75.92, -46.77) * mm, "end": v(-80.92, -46.77) * mm});
            skLineSegment(sketch, "E153.right", {"start": v(-80.92, -48.77) * mm, "end": v(-80.92, -46.77) * mm});
            skLineSegment(sketch, "E154", {"start": v(-75.92, -43.77) * mm, "end": v(-75.92, -46.77) * mm});
            skSolve(sketch);
        }
        {
            var Q0;
            Q0 = qSketchRegion(id + "F53", true);
            var Q1;
            Q1=sQuery(id+"F53.wireOp",EDGE,"E152.top");
            revolve(context, id + "F54", {"entities" : qUnion([Q0]), "axis" : qUnion([Q1]), "revolveType" : RevolveType.FULL});
        }
        {
            var Q0;
            Q0=makeQuery(id+"F3.opExtrude","CAP_FACE",FACE,{"disambiguationData":[OSD([sQuery(id+"F2.wireOp",EDGE,"E8.bottom"),sQuery(id+"F2.wireOp",EDGE,"E8.top"),sQuery(id+"F2.wireOp",EDGE,"E8.left"),sQuery(id+"F2.wireOp",EDGE,"E8.right")])],"isStart":false});
            var sketch = newSketch(context, id + "F55", { "sketchPlane" : qUnion([Q0])});
            skLineSegment(sketch, "E155", {"start": v(-91.92, -53.77) * mm, "end": v(-75.92, -53.77) * mm, "construction": true});
            skLineSegment(sketch, "E156", {"start": v(-75.92, -43.77) * mm, "end": v(-91.92, -43.77) * mm, "construction": true});
            skLineSegment(sketch, "E157.bottom", {"start": v(-91.92, -43.77) * mm, "end": v(-81.92, -43.77) * mm});
            skLineSegment(sketch, "E157.top", {"start": v(-91.92, -46.27) * mm, "end": v(-81.92, -46.27) * mm});
            skLineSegment(sketch, "E157.left", {"start": v(-91.92, -43.77) * mm, "end": v(-91.92, -46.27) * mm});
            skLineSegment(sketch, "E157.right", {"start": v(-81.92, -43.77) * mm, "end": v(-81.92, -46.27) * mm});
            skLineSegment(sketch, "E158.bottom", {"start": v(-91.92, -53.77) * mm, "end": v(-81.92, -53.77) * mm});
            skLineSegment(sketch, "E158.top", {"start": v(-91.92, -51.27) * mm, "end": v(-81.92, -51.27) * mm});
            skLineSegment(sketch, "E158.left", {"start": v(-91.92, -53.77) * mm, "end": v(-91.92, -51.27) * mm});
            skLineSegment(sketch, "E158.right", {"start": v(-81.92, -53.77) * mm, "end": v(-81.92, -51.27) * mm});
            skSolve(sketch);
        }
        {
            var Q0;
            Q0 = qSketchRegion(id + "F55", true);
            var Q1;
            Q1=makeQuery(id+"F54.opRevolve","SWEPT_FACE",FACE,{"disambiguationData":[OSD([sQuery(id+"F53.wireOp",EDGE,"E152.bottom")])]});
            extrude(context, id + "F56", {"entities" : qUnion([Q0]), "operationType" : NewBodyOperationType.REMOVE, "endBound" : BoundingType.UP_TO_SURFACE, "oppositeDirection" : true, "endBoundEntityFace" : qUnion([Q1]), "depth" : 25 * mm, "hasSecondDirection" : true, "secondDirectionOppositeDirection" : false, "secondDirectionDepth" : 25 * mm});
        }
        {
            var Q0;
            Q0=makeQuery(id+"F56.boolean.opBoolean","COPY",FACE,{"derivedFrom":makeQuery(id+"F56.opExtrude","SWEPT_FACE",FACE,{"disambiguationData":[OSD([sQuery(id+"F55.wireOp",EDGE,"E157.top")])]})});
            var sketch = newSketch(context, id + "F57", { "sketchPlane" : qUnion([Q0])});
            skLineSegment(sketch, "E159", {"start": v(91.92, 17) * mm, "end": v(75.92, 17) * mm, "construction": true});
            skLineSegment(sketch, "E160", {"start": v(75.92, 27) * mm, "end": v(91.92, 27) * mm, "construction": true});
            skArc(sketch, "E161", {"start": v(86.92, 17) * mm, "mid": v(91.92, 22) * mm, "end": v(86.92, 27) * mm});
            skLineSegment(sketch, "E162", {"start": v(91.92, 17) * mm, "end": v(91.92, 27) * mm, "construction": true});
            skCircle(sketch, "E163", {"center": v(86.92, 22) * mm, "radius": 2 * mm});
            skLineSegment(sketch, "E164", {"start": v(86.92, 17) * mm, "end": v(95.1, 17) * mm});
            skLineSegment(sketch, "E165", {"start": v(95.1, 17) * mm, "end": v(95.1, 27) * mm});
            skLineSegment(sketch, "E166", {"start": v(95.1, 27) * mm, "end": v(86.92, 27) * mm});
            skSolve(sketch);
        }
        {
            var Q0;
            Q0 = qSketchRegion(id + "F57", true);
            var Q1;
            Q1=makeQuery(id+"F56.boolean.opBoolean","COPY",FACE,{"derivedFrom":makeQuery(id+"F56.opExtrude","SWEPT_FACE",FACE,{"disambiguationData":[OSD([sQuery(id+"F55.wireOp",EDGE,"E158.top")])]})});
            extrude(context, id + "F58", {"entities" : qUnion([Q0]), "operationType" : NewBodyOperationType.REMOVE, "endBound" : BoundingType.UP_TO_SURFACE, "oppositeDirection" : true, "endBoundEntityFace" : qUnion([Q1]), "depth" : 25 * mm});
        }
        {
            var Q0;
            Q0=makeQuery(id+"F3.opExtrude","CAP_FACE",FACE,{"disambiguationData":[OSD([sQuery(id+"F2.wireOp",EDGE,"E8.bottom"),sQuery(id+"F2.wireOp",EDGE,"E8.top"),sQuery(id+"F2.wireOp",EDGE,"E8.left"),sQuery(id+"F2.wireOp",EDGE,"E8.right")])],"isStart":false});
            var sketch = newSketch(context, id + "F59", { "sketchPlane" : qUnion([Q0])});
            skLineSegment(sketch, "E167", {"start": v(-116.5, -47.8) * mm, "end": v(-211.5, -47.8) * mm});
            skLineSegment(sketch, "E168", {"start": v(-211.5, -47.8) * mm, "end": v(-211.5, -50.8) * mm});
            skLineSegment(sketch, "E169", {"start": v(-211.5, -50.8) * mm, "end": v(-121.5, -50.8) * mm});
            skLineSegment(sketch, "E170", {"start": v(-121.5, -50.8) * mm, "end": v(-121.5, -49.8) * mm});
            skLineSegment(sketch, "E171", {"start": v(-121.5, -49.8) * mm, "end": v(-116.5, -49.8) * mm});
            skLineSegment(sketch, "E172", {"start": v(-116.5, -49.8) * mm, "end": v(-116.5, -47.8) * mm});
            skSolve(sketch);
        }
        {
            var Q0;
            Q0 = qSketchRegion(id + "F59", true);
            var Q1;
            Q1=sQuery(id+"F59.wireOp",EDGE,"E167");
            revolve(context, id + "F60", {"entities" : qUnion([Q0]), "axis" : qUnion([Q1]), "revolveType" : RevolveType.FULL});
        }
        {
            var Q0;
            Q0=qCreatedBy(makeId("Top.planeOp"),FACE);
            var sketch = newSketch(context, id + "F61", { "sketchPlane" : qUnion([Q0])});
            skLineSegment(sketch, "E173.bottom", {"start": v(-80.95, -23.72) * mm, "end": v(-94.95, -23.72) * mm});
            skLineSegment(sketch, "E173.top", {"start": v(-80.95, -9.72) * mm, "end": v(-94.95, -9.72) * mm});
            skLineSegment(sketch, "E173.left", {"start": v(-80.95, -23.72) * mm, "end": v(-80.95, -9.72) * mm});
            skLineSegment(sketch, "E173.right", {"start": v(-94.95, -23.72) * mm, "end": v(-94.95, -19.22) * mm});
            skArc(sketch, "E174", {"start": v(-94.95, -19.22) * mm, "mid": v(-92.45, -16.72) * mm, "end": v(-94.95, -14.22) * mm});
            skLineSegment(sketch, "E175.trimOffspring", {"start": v(-94.95, -14.22) * mm, "end": v(-94.95, -9.72) * mm});
            skSolve(sketch);
        }
        {
            var Q0;
            Q0 = qSketchRegion(id + "F61", true);
            extrude(context, id + "F62", {"entities" : qUnion([Q0]), "depth" : 11 * mm});
        }
        {
            var Q0;
            Q0=makeQuery(id+"F62.opExtrude","SWEPT_FACE",FACE,{"disambiguationData":[OSD([sQuery(id+"F61.wireOp",EDGE,"E173.left")])]});
            var sketch = newSketch(context, id + "F63", { "sketchPlane" : qUnion([Q0])});
            skLineSegment(sketch, "E176", {"start": v(-23.72, 11) * mm, "end": v(-9.72, 0) * mm, "construction": true});
            skCircle(sketch, "E177", {"center": v(-16.72, 5.5) * mm, "radius": 3 * mm});
            skSolve(sketch);
        }
        {
            var Q0;
            Q0 = qSketchRegion(id + "F63", true);
            extrude(context, id + "F64", {"entities" : qUnion([Q0]), "operationType" : NewBodyOperationType.REMOVE, "oppositeDirection" : true, "depth" : 9 * mm});
        }
        {
            var Q0;
            Q0=makeQuery(id+"F62.opExtrude","SWEPT_FACE",FACE,{"disambiguationData":[OSD([sQuery(id+"F61.wireOp",EDGE,"E173.right")])]});
            var sketch = newSketch(context, id + "F65", { "sketchPlane" : qUnion([Q0])});
            skLineSegment(sketch, "E178.bottom", {"start": v(23.72, 11) * mm, "end": v(9.72, 11) * mm});
            skLineSegment(sketch, "E178.top", {"start": v(23.72, 0) * mm, "end": v(9.72, 0) * mm});
            skLineSegment(sketch, "E178.left", {"start": v(23.72, 11) * mm, "end": v(23.72, 0) * mm});
            skLineSegment(sketch, "E178.right", {"start": v(9.72, 11) * mm, "end": v(9.72, 0) * mm});
            skLineSegment(sketch, "E179", {"start": v(23.72, 0) * mm, "end": v(19.22, 11) * mm, "construction": true});
            skLineSegment(sketch, "E180", {"start": v(9.72, 0) * mm, "end": v(14.22, 11) * mm, "construction": true});
            skCircle(sketch, "E181", {"center": v(21.47, 5.5) * mm, "radius": 1 * mm});
            skCircle(sketch, "E182", {"center": v(11.97, 5.5) * mm, "radius": 1 * mm});
            skSolve(sketch);
        }
        {
            var Q0;
            Q0 = qSketchRegion(id + "F65", true);
            extrude(context, id + "F66", {"entities" : qUnion([Q0]), "depth" : 5 * mm});
        }
        {
            var Q0;
            Q0=makeQuery(id+"F66.opExtrude","SWEPT_FACE",FACE,{"disambiguationData":[OSD([sQuery(id+"F65.wireOp",EDGE,"E178.bottom")])]});
            var sketch = newSketch(context, id + "F67", { "sketchPlane" : qUnion([Q0])});
            skCircle(sketch, "E183", {"center": v(-94.95, -16.72) * mm, "radius": 2.5 * mm});
            skSolve(sketch);
        }
        {
            var Q0;
            Q0 = qSketchRegion(id + "F67", true);
            var Q1;
            Q1=makeQuery(id+"F66.opExtrude","SWEPT_FACE",FACE,{"disambiguationData":[OSD([sQuery(id+"F65.wireOp",EDGE,"E178.top")])]});
            extrude(context, id + "F68", {"entities" : qUnion([Q0]), "operationType" : NewBodyOperationType.REMOVE, "endBound" : BoundingType.UP_TO_SURFACE, "oppositeDirection" : true, "endBoundEntityFace" : qUnion([Q1]), "depth" : 25 * mm});
        }
        {
            var Q0;
            Q0=makeQuery(id+"F62.opExtrude","SWEPT_FACE",FACE,{"disambiguationData":[OSD([sQuery(id+"F61.wireOp",EDGE,"E173.right")])]});
            var sketch = newSketch(context, id + "F69", { "sketchPlane" : qUnion([Q0])});
            skCircle(sketch, "E184.0", {"center": v(21.47, 5.5) * mm, "radius": 1 * mm});
            skCircle(sketch, "E185.0", {"center": v(11.97, 5.5) * mm, "radius": 1 * mm});
            skSolve(sketch);
        }
        {
            var Q0;
            Q0 = qSketchRegion(id + "F69", true);
            extrude(context, id + "F70", {"entities" : qUnion([Q0]), "operationType" : NewBodyOperationType.REMOVE, "oppositeDirection" : true, "depth" : 10 * mm});
        }
        {
            var Q0;
            Q0=makeQuery(id+"F3.opExtrude","CAP_FACE",FACE,{"disambiguationData":[OSD([sQuery(id+"F2.wireOp",EDGE,"E8.bottom"),sQuery(id+"F2.wireOp",EDGE,"E8.top"),sQuery(id+"F2.wireOp",EDGE,"E8.left"),sQuery(id+"F2.wireOp",EDGE,"E8.right")])],"isStart":false});
            var sketch = newSketch(context, id + "F71", { "sketchPlane" : qUnion([Q0])});
            skLineSegment(sketch, "E186", {"start": v(-152.02, -13.08) * mm, "end": v(-152.02, 7.96) * mm, "construction": true});
            skLineSegment(sketch, "E187", {"start": v(-145.52, 7.96) * mm, "end": v(-93.52, 7.96) * mm});
            skLineSegment(sketch, "E188.0", {"start": v(-145.52, -16.04) * mm, "end": v(-145.52, 7.96) * mm});
            skLineSegment(sketch, "E189", {"start": v(-93.52, 7.96) * mm, "end": v(-93.52, 4.96) * mm});
            skLineSegment(sketch, "E190", {"start": v(-93.52, 4.96) * mm, "end": v(-140.52, 4.96) * mm});
            skLineSegment(sketch, "E191", {"start": v(-140.52, 4.96) * mm, "end": v(-140.52, -16.04) * mm});
            skLineSegment(sketch, "E192", {"start": v(-140.52, -16.04) * mm, "end": v(-145.52, -16.04) * mm});
            skLineSegment(sketch, "E193.MirrorCS", {"start": v(-158.52, -16.04) * mm, "end": v(-158.52, 7.96) * mm});
            skLineSegment(sketch, "E194.MirrorCS", {"start": v(-163.52, -16.04) * mm, "end": v(-158.52, -16.04) * mm});
            skLineSegment(sketch, "E195.MirrorCS", {"start": v(-163.52, 4.96) * mm, "end": v(-163.52, -16.04) * mm});
            skLineSegment(sketch, "E196.MirrorCS", {"start": v(-210.52, 4.96) * mm, "end": v(-163.52, 4.96) * mm});
            skLineSegment(sketch, "E197.MirrorCS", {"start": v(-210.52, 7.96) * mm, "end": v(-210.52, 4.96) * mm});
            skLineSegment(sketch, "E198.MirrorCS", {"start": v(-158.52, 7.96) * mm, "end": v(-210.52, 7.96) * mm});
            skPoint(sketch, "E199.orphan", {"position": v(-152.02, 7.96) * mm});
            skSolve(sketch);
        }
        {
            var Q0;
            Q0 = qSketchRegion(id + "F71", true);
            var Q1;
            Q1=sQuery(id+"F71.wireOp",EDGE,"E187");
            revolve(context, id + "F72", {"entities" : qUnion([Q0]), "axis" : qUnion([Q1]), "revolveType" : RevolveType.FULL});
        }
        {
            var Q0;
            Q0=makeQuery(id+"F72.opRevolve","SWEPT_FACE",FACE,{"disambiguationData":[OSD([sQuery(id+"F71.wireOp",EDGE,"E195.MirrorCS")])]});
            var sketch = newSketch(context, id + "F73", { "sketchPlane" : qUnion([Q0])});
            skLineSegment(sketch, "E200", {"start": v(-7.96, 22) * mm, "end": v(16.04, 22) * mm, "construction": true});
            skCircle(sketch, "E201", {"center": v(7.04, 22) * mm, "radius": 2.5 * mm});
            skSolve(sketch);
        }
        {
            var Q0;
            Q0 = qSketchRegion(id + "F73", true);
            var Q1;
            Q1=makeQuery(id+"F72.opRevolve","SWEPT_FACE",FACE,{"disambiguationData":[OSD([sQuery(id+"F71.wireOp",EDGE,"E188.0")])]});
            extrude(context, id + "F74", {"entities" : qUnion([Q0]), "operationType" : NewBodyOperationType.ADD, "endBound" : BoundingType.UP_TO_SURFACE, "oppositeDirection" : true, "endBoundEntityFace" : qUnion([Q1]), "depth" : 25 * mm});
        }
        {
            var Q0;
            Q0=makeQuery(id+"F72.opRevolve","SWEPT_FACE",FACE,{"disambiguationData":[OSD([sQuery(id+"F71.wireOp",EDGE,"E195.MirrorCS")])]});
            var sketch = newSketch(context, id + "F75", { "sketchPlane" : qUnion([Q0])});
            skLineSegment(sketch, "E202", {"start": v(-7.96, 22) * mm, "end": v(16.04, 22) * mm, "construction": true});
            skLineSegment(sketch, "E203", {"start": v(15.51, 17) * mm, "end": v(-23.83, 4) * mm});
            skLineSegment(sketch, "E204", {"start": v(-23.83, 4) * mm, "end": v(-23.83, -5.55) * mm});
            skLineSegment(sketch, "E205", {"start": v(-23.83, -5.55) * mm, "end": v(15.51, -5.55) * mm});
            skLineSegment(sketch, "E206", {"start": v(15.51, -5.55) * mm, "end": v(15.51, 17) * mm});
            skLineSegment(sketch, "E207.MirrorCS", {"start": v(15.51, 27) * mm, "end": v(-23.83, 40) * mm});
            skLineSegment(sketch, "E208.MirrorCS", {"start": v(15.51, 49.55) * mm, "end": v(15.51, 27) * mm});
            skLineSegment(sketch, "E209.MirrorCS", {"start": v(-23.83, 49.55) * mm, "end": v(15.51, 49.55) * mm});
            skLineSegment(sketch, "E210.MirrorCS", {"start": v(-23.83, 40) * mm, "end": v(-23.83, 49.55) * mm});
            skSolve(sketch);
        }
        {
            var Q0;
            Q0 = qSketchRegion(id + "F75", true);
            var Q1;
            Q1=makeQuery(id+"F72.opRevolve","SWEPT_FACE",FACE,{"disambiguationData":[OSD([sQuery(id+"F71.wireOp",EDGE,"E191")])]});
            extrude(context, id + "F76", {"entities" : qUnion([Q0]), "operationType" : NewBodyOperationType.REMOVE, "endBound" : BoundingType.UP_TO_SURFACE, "oppositeDirection" : true, "endBoundEntityFace" : qUnion([Q1]), "depth" : 25 * mm});
        }
        {
            var Q0;
            Q0=qCreatedBy(makeId("Top.planeOp"),FACE);
            var sketch = newSketch(context, id + "F77", { "sketchPlane" : qUnion([Q0])});
            skArc(sketch, "E211", {"start": v(-154.5, -88.24) * mm, "mid": v(-177, -72.59) * mm, "end": v(-199.5, -88.24) * mm});
            skArc(sketch, "E212", {"start": v(-184.07, -103.66) * mm, "mid": v(-177, -106.59) * mm, "end": v(-169.93, -103.66) * mm});
            skCircle(sketch, "E213", {"center": v(-177, -96.59) * mm, "radius": 3 * mm});
            skLineSegment(sketch, "E214", {"start": v(-169.93, -103.66) * mm, "end": v(-154.5, -88.24) * mm});
            skLineSegment(sketch, "E215", {"start": v(-177, -96.59) * mm, "end": v(-177, -72.59) * mm, "construction": true});
            skLineSegment(sketch, "E216.MirrorCS", {"start": v(-184.07, -103.66) * mm, "end": v(-199.5, -88.24) * mm});
            skSolve(sketch);
        }
        {
            var Q0;
            Q0 = qSketchRegion(id + "F77", true);
            extrude(context, id + "F78", {"entities" : qUnion([Q0]), "depth" : 3 * mm});
        }
        {
            var Q0;
            Q0=makeQuery(id+"F78.opExtrude","CAP_FACE",FACE,{"disambiguationData":[OSD([sQuery(id+"F77.wireOp",EDGE,"E211"),sQuery(id+"F77.wireOp",EDGE,"E212"),sQuery(id+"F77.wireOp",EDGE,"E213"),sQuery(id+"F77.wireOp",EDGE,"E214"),sQuery(id+"F77.wireOp",EDGE,"E216.MirrorCS")])],"isStart":false});
            var sketch = newSketch(context, id + "F79", { "sketchPlane" : qUnion([Q0])});
            skCircle(sketch, "E217", {"center": v(-177, -96.59) * mm, "radius": 10 * mm});
            skCircle(sketch, "E218.0", {"center": v(-177, -96.59) * mm, "radius": 3 * mm});
            skSolve(sketch);
        }
        {
            var Q0;
            Q0 = qSketchRegion(id + "F79", true);
            extrude(context, id + "F80", {"entities" : qUnion([Q0]), "operationType" : NewBodyOperationType.ADD, "depth" : 6 * mm});
        }
        {
            var Q0;
            Q0=makeQuery(id+"F80.opExtrude","CAP_FACE",FACE,{"disambiguationData":[OSD([sQuery(id+"F79.wireOp",EDGE,"E217"),sQuery(id+"F79.wireOp",EDGE,"E218.0")])],"isStart":false});
            cPlane(context, id + "F81", {"entities" : qUnion([Q0]), "cplaneType" : CPlaneType.OFFSET, "offset" : 3 * mm, "oppositeDirection" : true, "width" : 150 * mm, "height" : 150 * mm});
        }
        {
            var Q0;
            Q0=qCreatedBy(id+"F81.planeOp",FACE);
            var sketch = newSketch(context, id + "F82", { "sketchPlane" : qUnion([Q0])});
            skCircle(sketch, "E219.0.0", {"center": v(-177, -96.59) * mm, "radius": 10 * mm, "construction": true});
            skLineSegment(sketch, "E220.bottom", {"start": v(-177, -96.59) * mm, "end": v(-175, -96.59) * mm});
            skLineSegment(sketch, "E220.top", {"start": v(-177, -84.07) * mm, "end": v(-175, -84.07) * mm});
            skLineSegment(sketch, "E220.left", {"start": v(-177, -96.59) * mm, "end": v(-177, -84.07) * mm});
            skLineSegment(sketch, "E220.right", {"start": v(-175, -96.59) * mm, "end": v(-175, -84.07) * mm});
            skSolve(sketch);
        }
        {
            var Q0;
            Q0 = qSketchRegion(id + "F82", true);
            var Q1;
            Q1=sQuery(id+"F82.wireOp",EDGE,"E220.left");
            revolve(context, id + "F83", {"operationType" : NewBodyOperationType.REMOVE, "entities" : qUnion([Q0]), "axis" : qUnion([Q1]), "revolveType" : RevolveType.FULL, "oppositeDirection" : true});
        }
        {
            var Q0;
            Q0=qCreatedBy(makeId("Top.planeOp"),FACE);
            var sketch = newSketch(context, id + "F84", { "sketchPlane" : qUnion([Q0])});
            skCircle(sketch, "E221", {"center": v(-79.71, 60.27) * mm, "radius": 2 * mm});
            skCircle(sketch, "E222", {"center": v(-13.71, 60.27) * mm, "radius": 1 * mm});
            skCircle(sketch, "E223", {"center": v(-160.71, 60.27) * mm, "radius": 1.5 * mm});
            skLineSegment(sketch, "E224", {"start": v(-79.71, 65.27) * mm, "end": v(-79.71, 55.27) * mm, "construction": true});
            skArc(sketch, "E225", {"start": v(-160.78, 63.77) * mm, "mid": v(-164.21, 60.27) * mm, "end": v(-160.78, 56.77) * mm});
            skArc(sketch, "E226", {"start": v(-13.63, 56.77) * mm, "mid": v(-10.21, 60.27) * mm, "end": v(-13.63, 63.77) * mm});
            skLineSegment(sketch, "E227", {"start": v(-79.71, 65.27) * mm, "end": v(-160.78, 63.77) * mm});
            skLineSegment(sketch, "E228", {"start": v(-79.71, 55.27) * mm, "end": v(-160.78, 56.77) * mm});
            skLineSegment(sketch, "E229", {"start": v(-79.71, 65.27) * mm, "end": v(-13.63, 63.77) * mm});
            skLineSegment(sketch, "E230", {"start": v(-79.71, 55.27) * mm, "end": v(-13.63, 56.77) * mm});
            skSolve(sketch);
        }
        {
            var Q0;
            Q0 = qSketchRegion(id + "F84", true);
            extrude(context, id + "F85", {"entities" : qUnion([Q0]), "depth" : 2 * mm});
        }
        {
            var Q0;
            Q0=makeQuery(id+"F85.opExtrude","CAP_FACE",FACE,{"disambiguationData":[OSD([sQuery(id+"F84.wireOp",EDGE,"E221"),sQuery(id+"F84.wireOp",EDGE,"E222"),sQuery(id+"F84.wireOp",EDGE,"E223"),sQuery(id+"F84.wireOp",EDGE,"E225"),sQuery(id+"F84.wireOp",EDGE,"E226"),sQuery(id+"F84.wireOp",EDGE,"E227"),sQuery(id+"F84.wireOp",EDGE,"E228"),sQuery(id+"F84.wireOp",EDGE,"E229"),sQuery(id+"F84.wireOp",EDGE,"E230")])],"isStart":false});
            var sketch = newSketch(context, id + "F86", { "sketchPlane" : qUnion([Q0])});
            skLineSegment(sketch, "E231", {"start": v(-155.03, 63.88) * mm, "end": v(-155.03, 56.67) * mm});
            skArc(sketch, "E232.0", {"start": v(-160.78, 63.77) * mm, "mid": v(-164.21, 60.27) * mm, "end": v(-160.78, 56.77) * mm});
            skLineSegment(sketch, "E232.1", {"start": v(-155.03, 63.88) * mm, "end": v(-160.78, 63.77) * mm});
            skLineSegment(sketch, "E232.2", {"start": v(-155.03, 56.67) * mm, "end": v(-160.78, 56.77) * mm});
            skCircle(sketch, "E232.3", {"center": v(-160.71, 60.27) * mm, "radius": 1.5 * mm});
            skPoint(sketch, "E233.orphan", {"position": v(-79.71, 65.27) * mm});
            skPoint(sketch, "E234.orphan", {"position": v(-79.71, 55.27) * mm});
            skSolve(sketch);
        }
        {
            var Q0;
            Q0 = qSketchRegion(id + "F86", true);
            extrude(context, id + "F87", {"entities" : qUnion([Q0]), "operationType" : NewBodyOperationType.ADD, "depth" : 2 * mm});
        }
        {
            var Q0;
            Q0=makeQuery(id+"F87.opExtrude","CAP_FACE",FACE,{"disambiguationData":[OSD([sQuery(id+"F86.wireOp",EDGE,"E231"),sQuery(id+"F86.wireOp",EDGE,"E232.0"),sQuery(id+"F86.wireOp",EDGE,"E232.1"),sQuery(id+"F86.wireOp",EDGE,"E232.2"),sQuery(id+"F86.wireOp",EDGE,"E232.3")])],"isStart":false});
            var sketch = newSketch(context, id + "F88", { "sketchPlane" : qUnion([Q0])});
            skCircle(sketch, "E235", {"center": v(-160.71, 60.27) * mm, "radius": 5 * mm});
            skSolve(sketch);
        }
        {
            var Q0;
            Q0 = qSketchRegion(id + "F88", true);
            extrude(context, id + "F89", {"entities" : qUnion([Q0]), "depth" : 6 * mm});
        }
        {
            var Q0;
            Q0=makeQuery(id+"F89.opExtrude","CAP_FACE",FACE,{"disambiguationData":[OSD([sQuery(id+"F88.wireOp",EDGE,"E235")])],"isStart":true});
            var sketch = newSketch(context, id + "F90", { "sketchPlane" : qUnion([Q0])});
            skCircle(sketch, "E236.0", {"center": v(-160.71, -60.27) * mm, "radius": 1.5 * mm});
            skSolve(sketch);
        }
        {
            var Q0;
            Q0 = qSketchRegion(id + "F90", true);
            extrude(context, id + "F91", {"entities" : qUnion([Q0]), "operationType" : NewBodyOperationType.ADD, "depth" : 5 * mm});
        }
        {
            var Q0;
            Q0=qCreatedBy(makeId("Top.planeOp"),FACE);
            var sketch = newSketch(context, id + "F92", { "sketchPlane" : qUnion([Q0])});
            skCircle(sketch, "E237", {"center": v(14.75, 60.52) * mm, "radius": 3.5 * mm});
            skSolve(sketch);
        }
        {
            var Q0;
            Q0 = qSketchRegion(id + "F92", true);
            extrude(context, id + "F93", {"entities" : qUnion([Q0]), "depth" : 3 * mm});
        }
        {
            var Q0;
            Q0=makeQuery(id+"F93.opExtrude","CAP_FACE",FACE,{"disambiguationData":[OSD([sQuery(id+"F92.wireOp",EDGE,"E237")])],"isStart":false});
            var sketch = newSketch(context, id + "F94", { "sketchPlane" : qUnion([Q0])});
            skCircle(sketch, "E238", {"center": v(14.75, 60.52) * mm, "radius": 2 * mm});
            skSolve(sketch);
        }
        {
            var Q0;
            Q0 = qSketchRegion(id + "F94", true);
            extrude(context, id + "F95", {"entities" : qUnion([Q0]), "operationType" : NewBodyOperationType.ADD, "depth" : 2.1 * mm});
        }
        {
            var Q0;
            Q0=makeQuery(id+"F95.opExtrude","CAP_FACE",FACE,{"disambiguationData":[OSD([sQuery(id+"F94.wireOp",EDGE,"E238")])],"isStart":false});
            var sketch = newSketch(context, id + "F96", { "sketchPlane" : qUnion([Q0])});
            skCircle(sketch, "E239", {"center": v(14.75, 60.52) * mm, "radius": 1.5 * mm});
            skSolve(sketch);
        }
        {
            var Q0;
            Q0 = qSketchRegion(id + "F96", true);
            extrude(context, id + "F97", {"entities" : qUnion([Q0]), "operationType" : NewBodyOperationType.ADD, "depth" : 10 * mm});
        }
        {
            var Q0;
            Q0=makeQuery(id+"F93.opExtrude","CAP_FACE",FACE,{"disambiguationData":[OSD([sQuery(id+"F92.wireOp",EDGE,"E237")])],"isStart":true});
            var sketch = newSketch(context, id + "F98", { "sketchPlane" : qUnion([Q0])});
            skLineSegment(sketch, "E240.bottom", {"start": v(19.75, -59.77) * mm, "end": v(9.75, -59.77) * mm});
            skLineSegment(sketch, "E240.top", {"start": v(19.75, -61.27) * mm, "end": v(9.75, -61.27) * mm});
            skLineSegment(sketch, "E240.left", {"start": v(19.75, -59.77) * mm, "end": v(19.75, -61.27) * mm});
            skLineSegment(sketch, "E240.right", {"start": v(9.75, -59.77) * mm, "end": v(9.75, -61.27) * mm});
            skLineSegment(sketch, "E241", {"start": v(14.75, -60.52) * mm, "end": v(19.75, -60.52) * mm, "construction": true});
            skSolve(sketch);
        }
        {
            var Q0;
            Q0 = qSketchRegion(id + "F98", true);
            extrude(context, id + "F99", {"entities" : qUnion([Q0]), "operationType" : NewBodyOperationType.REMOVE, "oppositeDirection" : true, "depth" : 1.5 * mm});
        }
        {
            var Q0;
            Q0=qCreatedBy(makeId("Top.planeOp"),FACE);
            var sketch = newSketch(context, id + "F100", { "sketchPlane" : qUnion([Q0])});
            skLineSegment(sketch, "E242", {"start": v(21.1, 63.17) * mm, "end": v(71.1, 63.17) * mm, "construction": true});
            skLineSegment(sketch, "E243.bottom", {"start": v(39.1, 68.17) * mm, "end": v(21.1, 68.17) * mm});
            skLineSegment(sketch, "E243.top", {"start": v(39.1, 58.17) * mm, "end": v(21.1, 58.17) * mm});
            skLineSegment(sketch, "E243.left", {"start": v(39.1, 68.17) * mm, "end": v(39.1, 63.32) * mm});
            skLineSegment(sketch, "E243.right", {"start": v(21.1, 68.17) * mm, "end": v(21.1, 58.17) * mm});
            skCircle(sketch, "E244", {"center": v(28.1, 63.17) * mm, "radius": 2 * mm});
            skFitSpline(sketch, "E245", {"points": [v(39.1, 63.32) * mm, v(52.63, 63.17) * mm, v(59.86, 61.51) * mm, v(65.24, 56.93) * mm, v(69.17, 53) * mm, v(71.1, 53.71) * mm], "startDerivative": vector(34.47, -0.54) * mm, "endDerivative": vector(6.4, 13.29) * mm});
            skLineSegment(sketch, "E246", {"start": v(71.1, 63.17) * mm, "end": v(71.1, 53.71) * mm, "construction": true});
            skFitSpline(sketch, "E247.0", {"points": [v(39.1, 63.02) * mm, v(39.81, 63) * mm, v(41.51, 63) * mm, v(44.56, 63.02) * mm, v(47.28, 63.02) * mm, v(49.4, 63) * mm, v(50.96, 62.95) * mm, v(52.41, 62.89) * mm, v(53.73, 62.8) * mm, v(54.94, 62.67) * mm, v(56.4, 62.44) * mm, v(58.03, 62.03) * mm, v(59.78, 61.27) * mm, v(61.48, 60.2) * mm, v(62.84, 59.06) * mm, v(63.87, 58.04) * mm, v(64.61, 57.22) * mm, v(65.32, 56.37) * mm, v(66, 55.48) * mm, v(66.67, 54.63) * mm, v(67.34, 53.86) * mm, v(67.9, 53.33) * mm, v(68.38, 53) * mm, v(68.76, 52.81) * mm, v(69.15, 52.69) * mm, v(69.7, 52.63) * mm, v(70.33, 52.74) * mm, v(70.97, 53.06) * mm, v(71.27, 53.39) * mm, v(71.37, 53.58) * mm]});
            skLineSegment(sketch, "E248", {"start": v(71.37, 53.58) * mm, "end": v(71.1, 53.71) * mm});
            skLineSegment(sketch, "E249.trimOffspring", {"start": v(39.1, 63.02) * mm, "end": v(39.1, 58.17) * mm});
            skSolve(sketch);
        }
        {
            var Q0;
            Q0 = qSketchRegion(id + "F100", true);
            extrude(context, id + "F101", {"entities" : qUnion([Q0]), "depth" : 6 * mm});
        }
    });
